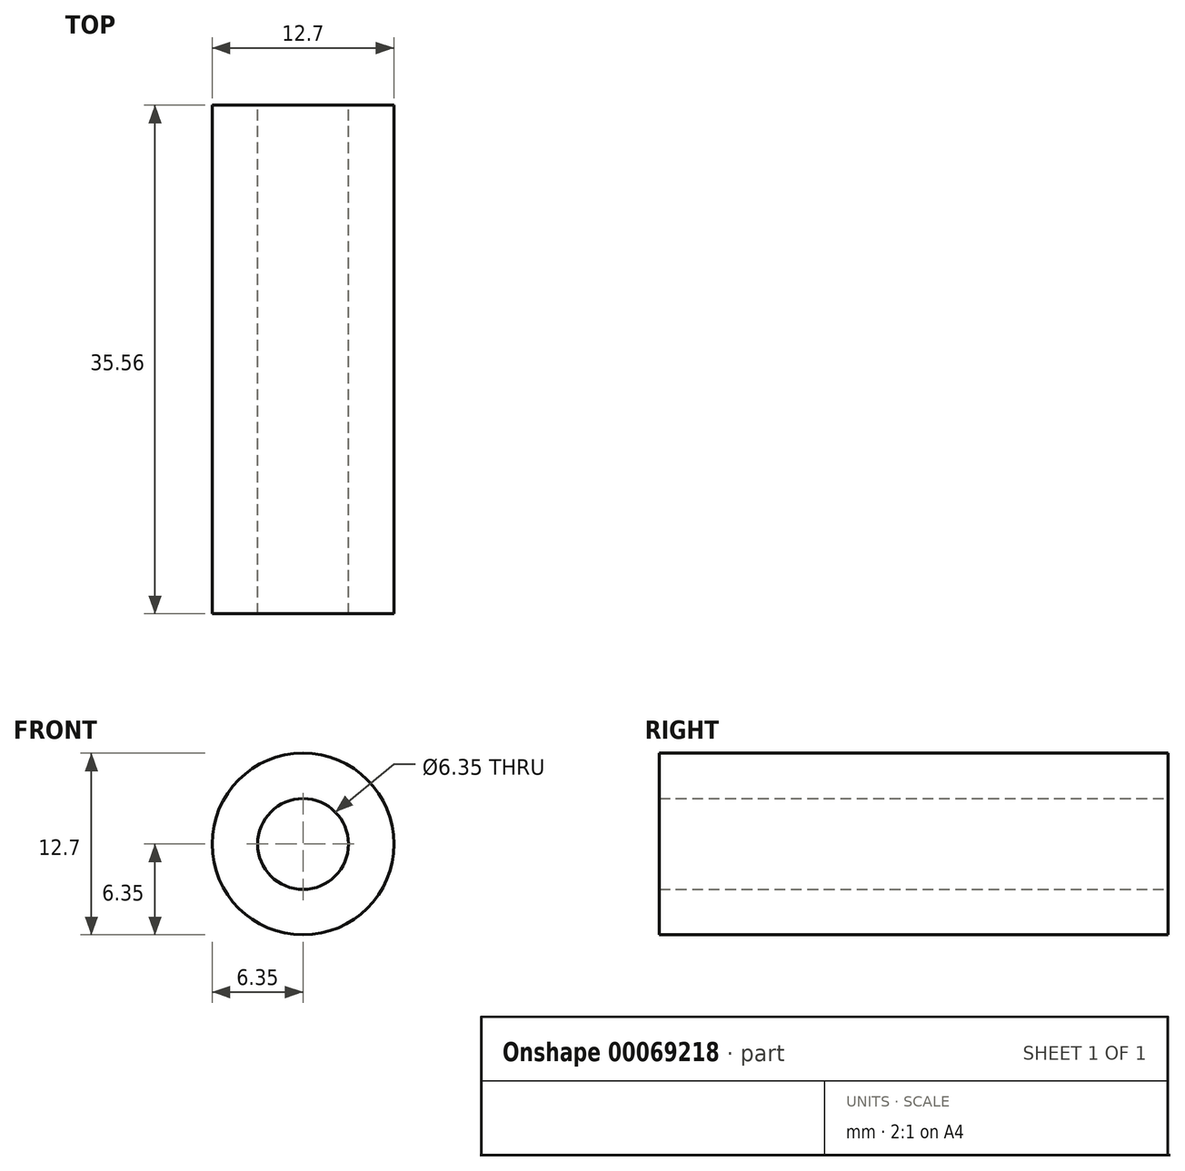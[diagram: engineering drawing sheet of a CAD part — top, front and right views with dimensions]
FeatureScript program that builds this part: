
annotation { "Feature Type Name" : "Feature", "Feature Type Description" : "" }
export const myFeature = defineFeature(function(context is Context, id is Id, definition is map)
    precondition{}
    {
        {
            var Q0;
            Q0=qCreatedBy(makeId("Front.planeOp"),FACE);
            var sketch = newSketch(context, id + "F0", { "sketchPlane" : qUnion([Q0])});
            skCircle(sketch, "E0", {"center": v(0, 0) * mm, "radius": 3.17 * mm});
            skCircle(sketch, "E1", {"center": v(0, 0) * mm, "radius": 6.35 * mm});
            skSolve(sketch);
        }
        {
            var Q0;
            Q0 = qSketchRegion(id + "F0", true);
            extrude(context, id + "F1", {"entities" : qUnion([Q0]), "depth" : 35.56 * mm});
        }
    });
